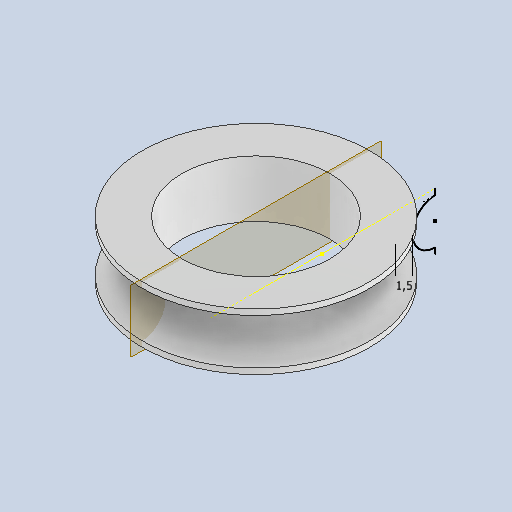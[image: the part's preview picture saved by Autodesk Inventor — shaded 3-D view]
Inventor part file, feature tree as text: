
AUTODESK INVENTOR PART (.ipt)
format: ipt  version: 2025 (Build 290162010, 162A)  size: 194,560 bytes
history: native  units: mm
features: other x4, sketch x3, reference x2, plane x1, sweep x1
ambient origin geometry x8: Origin, YZ Plane, XZ Plane, XY Plane, X Axis, Y Axis, Z Axis, Center Point
bodies: Body1 (feature_tree)
feature tree (11):
  sketch  "Skizze1"  dims[d0=20.0mm d4=1.5mm]
  sketch  "Skizze2"  dims[d7=0.0mm d8=0.0mm]
  plane  "Arbeitsebene1"
  sweep  "Sweeping2"
  reference  "Referenz1"
  sketch  "Skizze3"  dims[d9=8.0mm]
  reference  "Referenz2"
  other  "<userpath>\Documents\Inventor\Krandemonstrator\Umlenkrolle.iam"
  other  "Umlenkrolle.iam"
  other  "Lager:1"
  other  "BS 292: Teil 1 (I) (Metrisch) 624 - 4 x 13 x 5:1"
